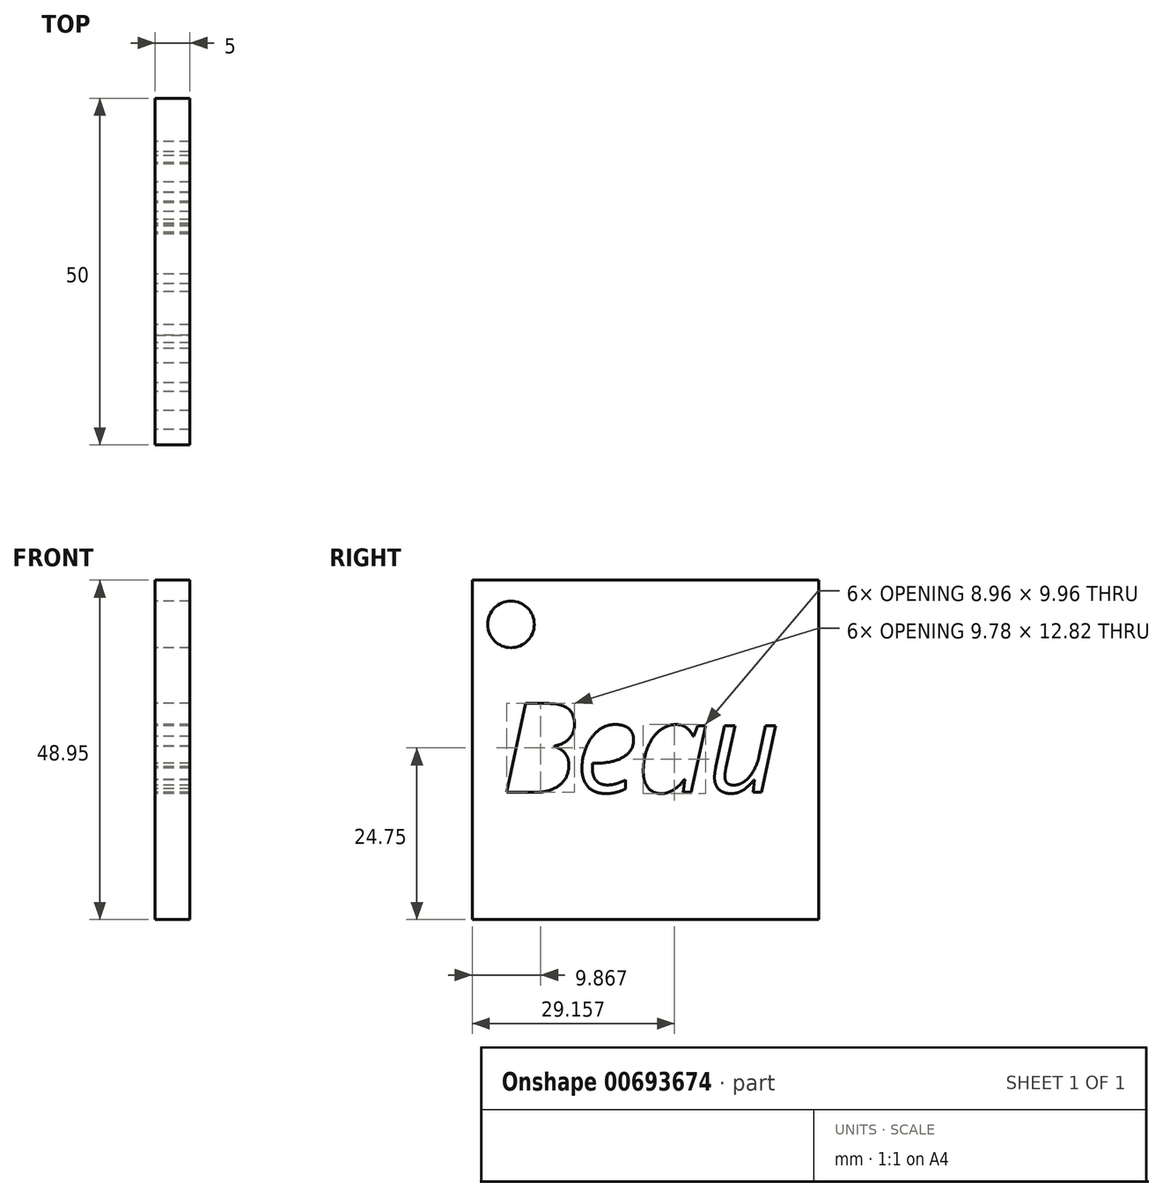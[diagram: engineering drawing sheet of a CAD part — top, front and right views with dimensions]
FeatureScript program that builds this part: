
annotation { "Feature Type Name" : "Feature", "Feature Type Description" : "" }
export const myFeature = defineFeature(function(context is Context, id is Id, definition is map)
    precondition{}
    {
        {
            var Q0;
            Q0=qCreatedBy(makeId("Right.planeOp"),FACE);
            var sketch = newSketch(context, id + "F0", { "sketchPlane" : qUnion([Q0])});
            skLineSegment(sketch, "E0.bottom", {"start": v(26.92, 22.46) * mm, "end": v(-23.08, 22.46) * mm});
            skLineSegment(sketch, "E0.top", {"start": v(26.92, -26.49) * mm, "end": v(-23.08, -26.49) * mm});
            skLineSegment(sketch, "E0.left", {"start": v(26.92, 22.46) * mm, "end": v(26.92, -26.49) * mm});
            skLineSegment(sketch, "E0.right", {"start": v(-23.08, 22.46) * mm, "end": v(-23.08, -26.49) * mm});
            skText(sketch, "E1", { "text": "Beau", "fontName": "OpenSans-Italic.ttf"});
            skCircle(sketch, "E2", {"center": v(-17.49, 16.07) * mm, "radius": 3.36 * mm});
            const initialGuessF0  = {"E1": [-0.01886, -0.00815, 1, 0, 0.01293]};
            skSetInitialGuess(sketch, initialGuessF0);
            skSolve(sketch);
        }
        {
            var Q0;
            Q0=makeQuery(id+"F0.imprint","IMPRINT",FACE,{"disambiguationData":[TD([[makeQuery(id+"F0.imprint","IMPRINT",EDGE,{"derivedFrom":sQuery(id+"F0.wireOp",EDGE,"E0.bottom")}),1.0]])]});
            extrude(context, id + "F1", {"entities" : qUnion([Q0]), "depth" : 5 * mm, "offsetDistance" : 25.4 * mm});
        }
    });
